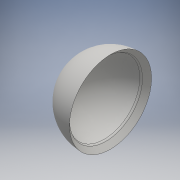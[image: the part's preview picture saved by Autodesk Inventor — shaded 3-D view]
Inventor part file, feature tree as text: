
AUTODESK INVENTOR PART (.ipt)
format: ipt  version: 2016 (Build 200138000, 138)  size: 141,312 bytes
history: native  units: mm
features: other x1, revolve x1, fillet x1, sketch x1
ambient origin geometry x8: Origin, YZ Plane, XZ Plane, XY Plane, X Axis, Y Axis, Z Axis, Center Point
bodies: Body1 (feature_tree)
feature tree (4):
  other  "ソリッド1"
  revolve  "回転1"
  fillet  "フィレット1"  Radius=25.0mm
  sketch  "スケッチ1"
